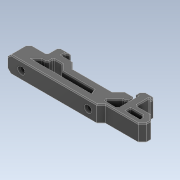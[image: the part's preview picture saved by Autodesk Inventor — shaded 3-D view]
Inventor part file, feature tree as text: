
AUTODESK INVENTOR PART (.ipt)
format: ipt  version: 2022.1 (Build 261234020, 234B)  size: 278,016 bytes
history: native  units: mm
features: chamfer x2, direct_edit x2, move_body x2, hole x1, sketch x1, other x1
ambient origin geometry x8: Origin, YZ Plane, XZ Plane, XY Plane, X Axis, Y Axis, Z Axis, Center Point
bodies: Volumenkörper1 (feature_tree)
feature tree (9):
  hole  "Bohrung1"  [1 undecoded]
  chamfer  "Fase1"  Distance=0.4mm
  direct_edit  "Direktbearbeitung1"
  direct_edit  "Direktbearbeitung2"
  chamfer  "Fase2"  Distance=0.4mm
  sketch  "Skizze1"  dims[d0=2.82mm d1=6.0mm d2=4.7mm d3=5.0mm d4=90.0deg d5=6.0mm d6=0.0mm d7=0.3mm d8=1.0mm d9=45.0deg d10=0.0mm d11=0.0mm d12=0.4mm d13=0.0mm d14=0.0mm d15=0.4mm d16=0.46mm d17=1.2mm d18=45.0deg]
  other  "pcb_din_clip_v2"
  move_body  "Verschieben1"
  move_body  "Verschieben2"
note: 1 required parameter value undecoded (feature->parameter linkage not recoverable at this tier; creation-order binding heuristic only, values carry confidence <= 0.55)
